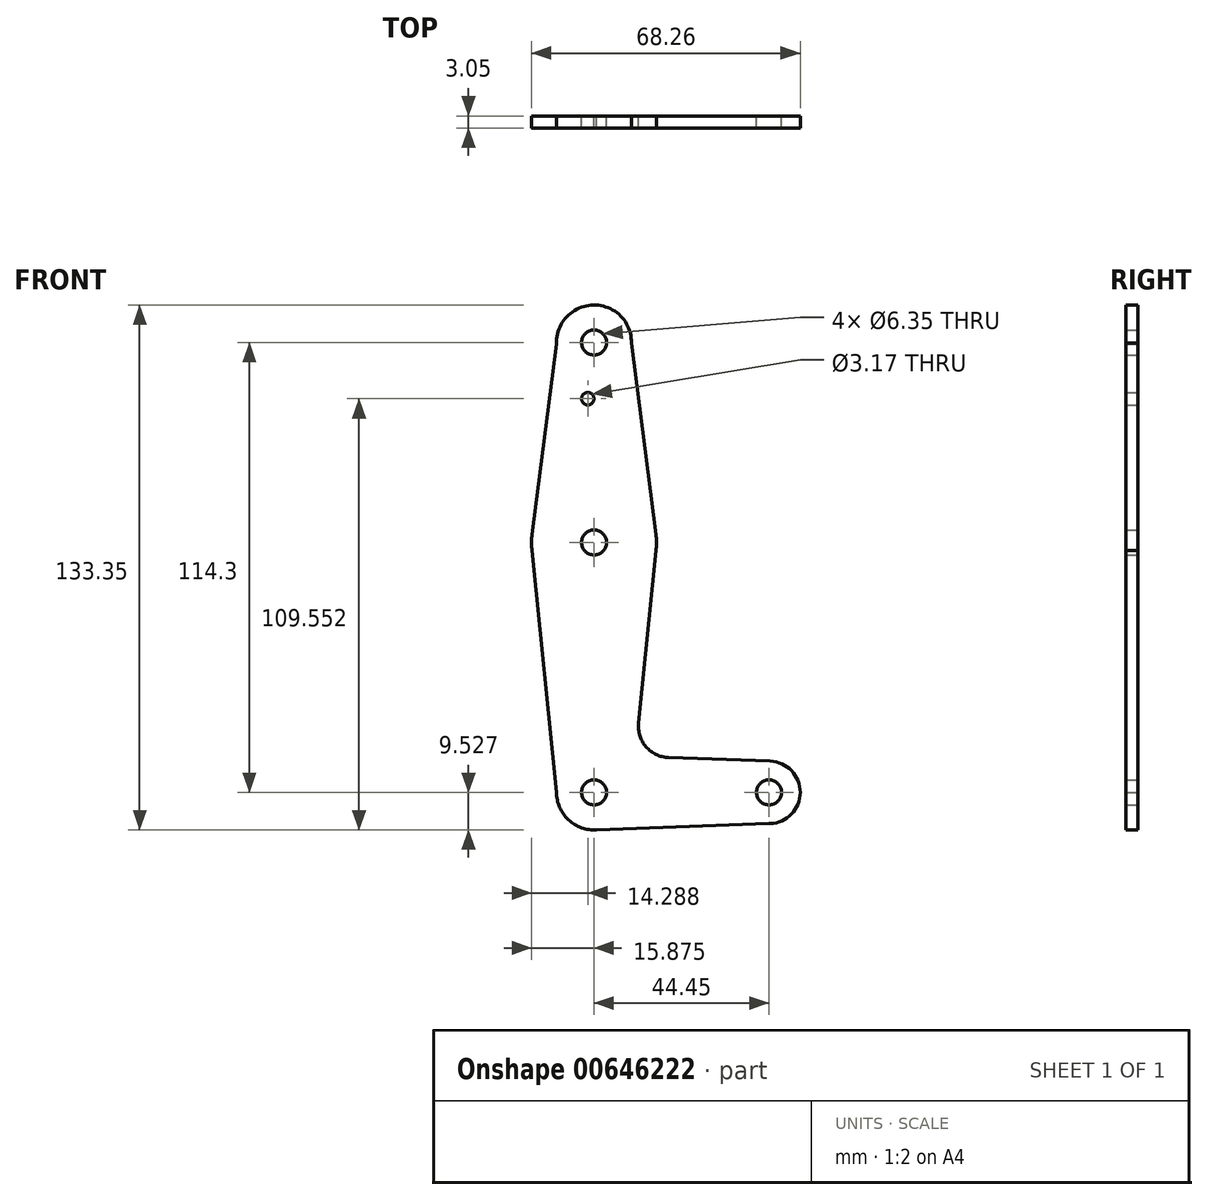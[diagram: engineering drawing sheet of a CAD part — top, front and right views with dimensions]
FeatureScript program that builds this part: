
annotation { "Feature Type Name" : "Feature", "Feature Type Description" : "" }
export const myFeature = defineFeature(function(context is Context, id is Id, definition is map)
    precondition{}
    {
        {
            var Q0;
            Q0=qCreatedBy(makeId("Front.planeOp"),FACE);
            var sketch = newSketch(context, id + "F0", { "sketchPlane" : qUnion([Q0])});
            skPoint(sketch, "E0.center.orphan", {"position": v(0, 60.51) * mm});
            skLineSegment(sketch, "E1", {"start": v(27.55, 97.64) * mm, "end": v(27.55, -16.66) * mm, "construction": true});
            skLineSegment(sketch, "E2", {"start": v(27.55, -16.66) * mm, "end": v(72, -16.66) * mm});
            skCircle(sketch, "E3", {"center": v(27.55, 97.64) * mm, "radius": 9.53 * mm});
            skCircle(sketch, "E4", {"center": v(27.55, 46.84) * mm, "radius": 15.88 * mm});
            skCircle(sketch, "E5", {"center": v(72, -16.66) * mm, "radius": 7.94 * mm});
            skLineSegment(sketch, "E6", {"start": v(18.03, 97.26) * mm, "end": v(11.8, 48.86) * mm});
            skLineSegment(sketch, "E7", {"start": v(37.07, 97.53) * mm, "end": v(43.3, 48.85) * mm});
            skLineSegment(sketch, "E8", {"start": v(11.8, 44.81) * mm, "end": v(18.02, -16.64) * mm});
            skLineSegment(sketch, "E9", {"start": v(46.48, -7.81) * mm, "end": v(72.28, -8.73) * mm});
            skLineSegment(sketch, "E10", {"start": v(43.3, 44.82) * mm, "end": v(38.85, 0.93) * mm});
            skCircle(sketch, "E11", {"center": v(27.55, 97.64) * mm, "radius": 3.18 * mm});
            skCircle(sketch, "E12", {"center": v(27.55, 46.84) * mm, "radius": 3.18 * mm});
            skCircle(sketch, "E13", {"center": v(27.55, -16.66) * mm, "radius": 3.18 * mm});
            skCircle(sketch, "E14", {"center": v(72, -16.66) * mm, "radius": 3.18 * mm});
            skArc(sketch, "E15.filletArc", {"start": v(38.85, 0.93) * mm, "mid": v(40.77, -5.1) * mm, "end": v(46.48, -7.81) * mm});
            skCircle(sketch, "E16", {"center": v(25.96, 83.36) * mm, "radius": 1.59 * mm});
            skPoint(sketch, "E17.orphan", {"position": v(72, -24.6) * mm});
            skLineSegment(sketch, "E18", {"start": v(72.28, -24.6) * mm, "end": v(72, -24.6) * mm});
            skPoint(sketch, "E19.start.orphan", {"position": v(27.55, -26.19) * mm});
            skCircle(sketch, "E20", {"center": v(27.55, -16.66) * mm, "radius": 9.53 * mm});
            skLineSegment(sketch, "E21", {"start": v(27.55, -26.19) * mm, "end": v(72, -24.6) * mm});
            skSolve(sketch);
        }
        {
            var Q0;
            Q0 = qSketchRegion(id + "F0", true);
            extrude(context, id + "F1", {"entities" : qUnion([Q0]), "depth" : 3.05 * mm, "offsetDistance" : 25.4 * mm});
        }
    });
